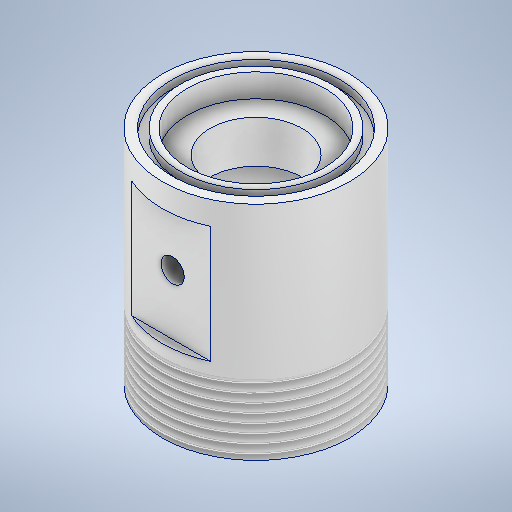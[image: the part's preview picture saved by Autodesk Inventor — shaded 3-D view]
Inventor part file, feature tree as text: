
AUTODESK INVENTOR PART (.ipt)
format: ipt  version: 2025 (Build 290162000, 162)  size: 379,392 bytes
history: native  units: in
note: dims shown in document units (in); Inventor stores cm internally (conversion verified against a paired STEP export)
features: sketch x7, extrude x5, thread x1, revolve x1, hole x1
ambient origin geometry x8: Origin, YZ Plane, XZ Plane, XY Plane, X Axis, Y Axis, Z Axis, Center Point
bodies: Solid1 (feature_tree)
feature tree (15):
  extrude  "Extrusion1"  Depth=1.4961in TaperAngle=0.0deg
  thread  "Thread1"  [1 undecoded]
  extrude  "Extrusion2"  TaperAngle=0.0deg  [1 undecoded]
  extrude  "Extrusion3"  Depth=0.1575in TaperAngle=0.0deg
  extrude  "Extrusion4"  Depth=0.0591in
  revolve  "Revolution1"  [1 undecoded]
  hole  "Hole1"  [1 undecoded]
  extrude  "Extrusion5"  Depth=0.0787in
  sketch  "Sketch1"  dims[d0=1.2598in d1=1.4961in d2=0.0in d3=0.4724in d4=0.0in]
  sketch  "Sketch2"  dims[d5=0.6201in d6=0.0in d7=0.0in]
  sketch  "Sketch3"  dims[d8=0.9252in d9=0.1575in d10=0.0in]
  sketch  "Sketch4"  dims[d11=0.7874in d12=0.0591in]
  sketch  "Sketch5"  dims[d13=0.0591in d14=0.0in d15=0.0in]
  sketch  "Sketch6"  dims[d16=90.0deg d17=0.4429in]
  sketch  "Sketch7"  dims[d18=0.6398in d19=0.0787in d20=0.1969in d21=0.0984in d22=0.1575in d23=2.3622in d24=0.1575in d25=0.0787in d26=90.0deg d27=0.315in d28=0.8108in d29=0.0472in d30=0.0551in d31=0.0551in d32=0.0in d33=0.1575in]
note: 4 required parameter values undecoded (feature->parameter linkage not recoverable at this tier; creation-order binding heuristic only, values carry confidence <= 0.55)